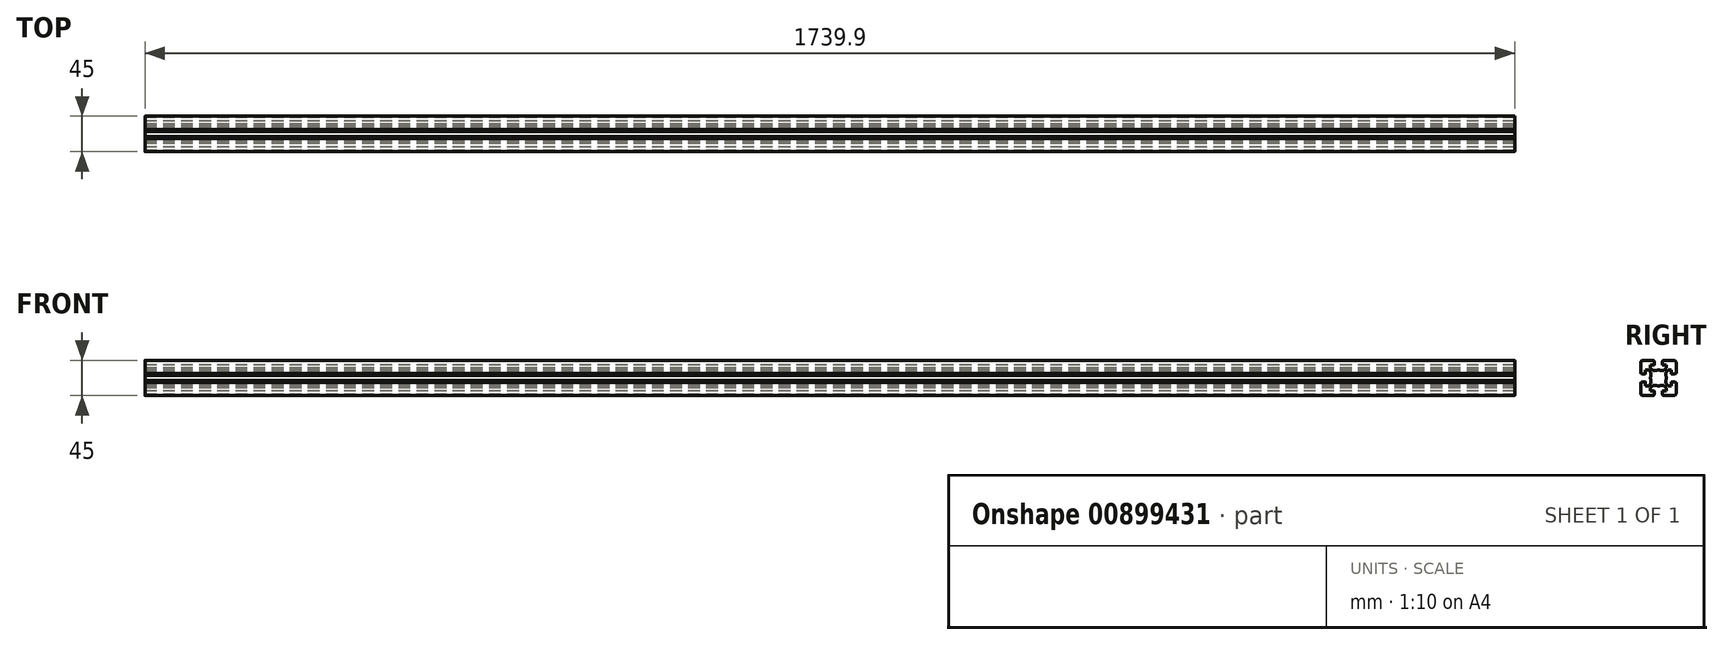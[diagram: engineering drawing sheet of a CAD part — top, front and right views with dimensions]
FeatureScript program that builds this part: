
annotation { "Feature Type Name" : "Feature", "Feature Type Description" : "" }
export const myFeature = defineFeature(function(context is Context, id is Id, definition is map)
    precondition{}
    {
        {
            var Q0;
            Q0=qCreatedBy(makeId("Right.planeOp"),FACE);
            var sketch = newSketch(context, id + "F0", { "sketchPlane" : qUnion([Q0])});
            skLineSegment(sketch, "E0", {"start": v(-20.09, -10.29) * mm, "end": v(-21.29, -10.29) * mm});
            skArc(sketch, "E1", {"start": v(-21.29, -10.29) * mm, "mid": v(-21.5, -10.38) * mm, "end": v(-21.59, -10.59) * mm});
            skLineSegment(sketch, "E2", {"start": v(-21.59, -10.59) * mm, "end": v(-21.59, -23.99) * mm});
            skArc(sketch, "E3", {"start": v(-21.59, -23.99) * mm, "mid": v(-20.7, -26.11) * mm, "end": v(-18.59, -26.99) * mm});
            skLineSegment(sketch, "E4", {"start": v(-18.59, -26.99) * mm, "end": v(-5.19, -26.99) * mm});
            skArc(sketch, "E5", {"start": v(-5.19, -26.99) * mm, "mid": v(-4.98, -26.9) * mm, "end": v(-4.89, -26.69) * mm});
            skLineSegment(sketch, "E6", {"start": v(-4.89, -26.69) * mm, "end": v(-4.89, -25.49) * mm});
            skLineSegment(sketch, "E7", {"start": v(-4.89, -25.49) * mm, "end": v(-4.39, -25.49) * mm});
            skArc(sketch, "E8", {"start": v(-4.39, -25.49) * mm, "mid": v(-4.18, -25.4) * mm, "end": v(-4.09, -25.19) * mm});
            skLineSegment(sketch, "E9", {"start": v(-4.09, -25.19) * mm, "end": v(-4.09, -21.29) * mm});
            skArc(sketch, "E10", {"start": v(-4.09, -21.29) * mm, "mid": v(-4.18, -21.08) * mm, "end": v(-4.39, -20.99) * mm});
            skLineSegment(sketch, "E11", {"start": v(-4.39, -20.99) * mm, "end": v(-9.14, -20.99) * mm});
            skLineSegment(sketch, "E12", {"start": v(-9.14, -20.99) * mm, "end": v(-9.14, -16.88) * mm});
            skLineSegment(sketch, "E13", {"start": v(-9.14, -16.88) * mm, "end": v(-6.25, -13.99) * mm});
            skLineSegment(sketch, "E14", {"start": v(-6.25, -13.99) * mm, "end": v(-2.21, -13.99) * mm});
            skArc(sketch, "E15", {"start": v(-2.21, -13.99) * mm, "mid": v(0.91, -14.49) * mm, "end": v(4.03, -13.99) * mm});
            skLineSegment(sketch, "E16", {"start": v(-20.09, -10.29) * mm, "end": v(-20.09, -9.79) * mm});
            skArc(sketch, "E17", {"start": v(-20.09, -9.79) * mm, "mid": v(-20, -9.58) * mm, "end": v(-19.79, -9.49) * mm});
            skLineSegment(sketch, "E18", {"start": v(-19.79, -9.49) * mm, "end": v(-15.89, -9.49) * mm});
            skArc(sketch, "E19", {"start": v(-15.89, -9.49) * mm, "mid": v(-15.68, -9.58) * mm, "end": v(-15.59, -9.79) * mm});
            skLineSegment(sketch, "E20", {"start": v(-15.59, -9.79) * mm, "end": v(-15.59, -14.54) * mm});
            skLineSegment(sketch, "E21", {"start": v(-15.59, -14.54) * mm, "end": v(-11.48, -14.54) * mm});
            skLineSegment(sketch, "E22", {"start": v(-11.48, -14.54) * mm, "end": v(-8.59, -11.65) * mm});
            skLineSegment(sketch, "E23", {"start": v(-8.59, -11.65) * mm, "end": v(-8.59, -7.61) * mm});
            skLineSegment(sketch, "E24", {"start": v(29.82, -4.49) * mm, "end": v(-31.05, -4.49) * mm});
            skLineSegment(sketch, "E25.MirrorCS", {"start": v(6.71, -25.49) * mm, "end": v(6.21, -25.49) * mm});
            skArc(sketch, "E26.MirrorCS", {"start": v(7.01, -26.99) * mm, "mid": v(6.8, -26.9) * mm, "end": v(6.71, -26.69) * mm});
            skLineSegment(sketch, "E27.MirrorCS", {"start": v(10.41, -11.65) * mm, "end": v(10.41, -7.61) * mm});
            skArc(sketch, "E28.MirrorCS", {"start": v(6.21, -25.49) * mm, "mid": v(6, -25.4) * mm, "end": v(5.91, -25.19) * mm});
            skLineSegment(sketch, "E29.MirrorCS", {"start": v(6.71, -26.69) * mm, "end": v(6.71, -25.49) * mm});
            skArc(sketch, "E30.MirrorCS", {"start": v(5.91, -21.29) * mm, "mid": v(6, -21.08) * mm, "end": v(6.21, -20.99) * mm});
            skLineSegment(sketch, "E31.MirrorCS", {"start": v(10.96, -16.88) * mm, "end": v(8.07, -13.99) * mm});
            skLineSegment(sketch, "E32.MirrorCS", {"start": v(13.3, -14.54) * mm, "end": v(10.41, -11.65) * mm});
            skLineSegment(sketch, "E33.MirrorCS", {"start": v(17.41, -14.54) * mm, "end": v(13.3, -14.54) * mm});
            skLineSegment(sketch, "E34.MirrorCS", {"start": v(17.41, -9.79) * mm, "end": v(17.41, -14.54) * mm});
            skLineSegment(sketch, "E35.MirrorCS", {"start": v(6.21, -20.99) * mm, "end": v(10.96, -20.99) * mm});
            skLineSegment(sketch, "E36.MirrorCS", {"start": v(8.07, -13.99) * mm, "end": v(4.03, -13.99) * mm});
            skArc(sketch, "E37.MirrorCS", {"start": v(4.03, -13.99) * mm, "mid": v(0.91, -14.49) * mm, "end": v(-2.21, -13.99) * mm});
            skLineSegment(sketch, "E38.MirrorCS", {"start": v(10.96, -20.99) * mm, "end": v(10.96, -16.88) * mm});
            skLineSegment(sketch, "E39.MirrorCS", {"start": v(5.91, -25.19) * mm, "end": v(5.91, -21.29) * mm});
            skArc(sketch, "E40.MirrorCS", {"start": v(23.41, -23.99) * mm, "mid": v(22.53, -26.11) * mm, "end": v(20.41, -26.99) * mm});
            skLineSegment(sketch, "E41.MirrorCS", {"start": v(20.41, -26.99) * mm, "end": v(7.01, -26.99) * mm});
            skLineSegment(sketch, "E42.MirrorCS", {"start": v(23.41, -10.59) * mm, "end": v(23.41, -23.99) * mm});
            skArc(sketch, "E43.MirrorCS", {"start": v(17.71, -9.49) * mm, "mid": v(17.5, -9.58) * mm, "end": v(17.41, -9.79) * mm});
            skArc(sketch, "E44.MirrorCS", {"start": v(23.11, -10.29) * mm, "mid": v(23.32, -10.38) * mm, "end": v(23.41, -10.59) * mm});
            skLineSegment(sketch, "E45.MirrorCS", {"start": v(21.91, -10.29) * mm, "end": v(21.91, -9.79) * mm});
            skLineSegment(sketch, "E46.MirrorCS", {"start": v(21.91, -10.29) * mm, "end": v(23.11, -10.29) * mm});
            skArc(sketch, "E47.MirrorCS", {"start": v(21.91, -9.79) * mm, "mid": v(21.82, -9.58) * mm, "end": v(21.61, -9.49) * mm});
            skLineSegment(sketch, "E48.MirrorCS", {"start": v(21.61, -9.49) * mm, "end": v(17.71, -9.49) * mm});
            skLineSegment(sketch, "E49.MirrorCS", {"start": v(6.71, 16.51) * mm, "end": v(6.21, 16.51) * mm});
            skArc(sketch, "E50.MirrorCS", {"start": v(-4.39, 16.51) * mm, "mid": v(-4.18, 16.42) * mm, "end": v(-4.09, 16.21) * mm});
            skLineSegment(sketch, "E51.MirrorCS", {"start": v(-4.89, 16.51) * mm, "end": v(-4.39, 16.51) * mm});
            skArc(sketch, "E52.MirrorCS", {"start": v(5.91, 12.31) * mm, "mid": v(6, 12.1) * mm, "end": v(6.21, 12.01) * mm});
            skLineSegment(sketch, "E53.MirrorCS", {"start": v(6.71, 17.71) * mm, "end": v(6.71, 16.51) * mm});
            skLineSegment(sketch, "E54.MirrorCS", {"start": v(-4.89, 17.71) * mm, "end": v(-4.89, 16.51) * mm});
            skArc(sketch, "E55.MirrorCS", {"start": v(-5.19, 18.01) * mm, "mid": v(-4.98, 17.92) * mm, "end": v(-4.89, 17.71) * mm});
            skArc(sketch, "E56.MirrorCS", {"start": v(-4.09, 12.31) * mm, "mid": v(-4.18, 12.1) * mm, "end": v(-4.39, 12.01) * mm});
            skArc(sketch, "E57.MirrorCS", {"start": v(7.01, 18.01) * mm, "mid": v(6.8, 17.92) * mm, "end": v(6.71, 17.71) * mm});
            skArc(sketch, "E58.MirrorCS", {"start": v(6.21, 16.51) * mm, "mid": v(6, 16.42) * mm, "end": v(5.91, 16.21) * mm});
            skArc(sketch, "E59.MirrorCS", {"start": v(23.11, 1.31) * mm, "mid": v(23.32, 1.4) * mm, "end": v(23.41, 1.61) * mm});
            skLineSegment(sketch, "E60.MirrorCS", {"start": v(21.91, 1.31) * mm, "end": v(21.91, 0.81) * mm});
            skArc(sketch, "E61.MirrorCS", {"start": v(-15.89, 0.51) * mm, "mid": v(-15.68, 0.6) * mm, "end": v(-15.59, 0.81) * mm});
            skArc(sketch, "E62.MirrorCS", {"start": v(-21.29, 1.31) * mm, "mid": v(-21.5, 1.4) * mm, "end": v(-21.59, 1.61) * mm});
            skArc(sketch, "E63.MirrorCS", {"start": v(17.71, 0.51) * mm, "mid": v(17.5, 0.6) * mm, "end": v(17.41, 0.81) * mm});
            skArc(sketch, "E64.MirrorCS", {"start": v(21.91, 0.81) * mm, "mid": v(21.82, 0.6) * mm, "end": v(21.61, 0.51) * mm});
            skLineSegment(sketch, "E65.MirrorCS", {"start": v(21.91, 1.31) * mm, "end": v(23.11, 1.31) * mm});
            skArc(sketch, "E66.MirrorCS", {"start": v(14.31, 5.31) * mm, "mid": v(14.1, 5.4) * mm, "end": v(14.01, 5.61) * mm});
            skArc(sketch, "E67.MirrorCS", {"start": v(-20.09, 0.81) * mm, "mid": v(-20, 0.6) * mm, "end": v(-19.79, 0.51) * mm});
            skLineSegment(sketch, "E68.MirrorCS", {"start": v(-20.09, 1.31) * mm, "end": v(-21.29, 1.31) * mm});
            skLineSegment(sketch, "E69.MirrorCS", {"start": v(-20.09, 1.31) * mm, "end": v(-20.09, 0.81) * mm});
            skLineSegment(sketch, "E70.MirrorCS", {"start": v(8.07, 5.01) * mm, "end": v(4.03, 5.01) * mm});
            skLineSegment(sketch, "E71.MirrorCS", {"start": v(-4.09, 16.21) * mm, "end": v(-4.09, 12.31) * mm});
            skLineSegment(sketch, "E72.MirrorCS", {"start": v(-9.14, 12.01) * mm, "end": v(-9.14, 7.9) * mm});
            skLineSegment(sketch, "E73.MirrorCS", {"start": v(-15.59, 5.56) * mm, "end": v(-11.48, 5.56) * mm});
            skLineSegment(sketch, "E74.MirrorCS", {"start": v(-4.39, 12.01) * mm, "end": v(-9.14, 12.01) * mm});
            skLineSegment(sketch, "E75.MirrorCS", {"start": v(-9.14, 7.9) * mm, "end": v(-6.25, 5.01) * mm});
            skLineSegment(sketch, "E76.MirrorCS", {"start": v(10.96, 12.01) * mm, "end": v(10.96, 7.9) * mm});
            skArc(sketch, "E77.MirrorCS", {"start": v(-21.59, 15.01) * mm, "mid": v(-20.7, 17.13) * mm, "end": v(-18.59, 18.01) * mm});
            skLineSegment(sketch, "E78.MirrorCS", {"start": v(23.41, 1.61) * mm, "end": v(23.41, 15.01) * mm});
            skLineSegment(sketch, "E79.MirrorCS", {"start": v(13.3, 5.56) * mm, "end": v(10.41, 2.67) * mm});
            skLineSegment(sketch, "E80.MirrorCS", {"start": v(-8.59, 2.67) * mm, "end": v(-8.59, -1.37) * mm});
            skLineSegment(sketch, "E81.MirrorCS", {"start": v(-15.59, 0.81) * mm, "end": v(-15.59, 5.56) * mm});
            skLineSegment(sketch, "E82.MirrorCS", {"start": v(10.41, 2.67) * mm, "end": v(10.41, -1.37) * mm});
            skLineSegment(sketch, "E83.MirrorCS", {"start": v(-18.59, 18.01) * mm, "end": v(-5.19, 18.01) * mm});
            skLineSegment(sketch, "E84.MirrorCS", {"start": v(10.96, 7.9) * mm, "end": v(8.07, 5.01) * mm});
            skLineSegment(sketch, "E85.MirrorCS", {"start": v(17.41, 5.56) * mm, "end": v(13.3, 5.56) * mm});
            skArc(sketch, "E86.MirrorCS", {"start": v(23.41, 15.01) * mm, "mid": v(22.53, 17.13) * mm, "end": v(20.41, 18.01) * mm});
            skLineSegment(sketch, "E87.MirrorCS", {"start": v(5.91, 16.21) * mm, "end": v(5.91, 12.31) * mm});
            skLineSegment(sketch, "E88.MirrorCS", {"start": v(17.41, 0.81) * mm, "end": v(17.41, 5.56) * mm});
            skLineSegment(sketch, "E89.MirrorCS", {"start": v(-11.48, 5.56) * mm, "end": v(-8.59, 2.67) * mm});
            skLineSegment(sketch, "E90.MirrorCS", {"start": v(-6.25, 5.01) * mm, "end": v(-2.21, 5.01) * mm});
            skLineSegment(sketch, "E91.MirrorCS", {"start": v(-21.59, 1.61) * mm, "end": v(-21.59, 15.01) * mm});
            skArc(sketch, "E92.MirrorCS", {"start": v(4.03, 5.01) * mm, "mid": v(0.91, 5.51) * mm, "end": v(-2.21, 5.01) * mm});
            skLineSegment(sketch, "E93.MirrorCS", {"start": v(6.21, 12.01) * mm, "end": v(10.96, 12.01) * mm});
            skArc(sketch, "E94.MirrorCS", {"start": v(-2.21, 5.01) * mm, "mid": v(0.91, 5.51) * mm, "end": v(4.03, 5.01) * mm});
            skLineSegment(sketch, "E95.MirrorCS", {"start": v(20.41, 18.01) * mm, "end": v(7.01, 18.01) * mm});
            skLineSegment(sketch, "E96.MirrorCS", {"start": v(-19.79, 0.51) * mm, "end": v(-15.89, 0.51) * mm});
            skLineSegment(sketch, "E97.MirrorCS", {"start": v(21.61, 0.51) * mm, "end": v(17.71, 0.51) * mm});
            skLineSegment(sketch, "E98.MirrorCS", {"start": v(0.91, -27.65) * mm, "end": v(0.91, 19.82) * mm});
            skArc(sketch, "E99", {"start": v(-8.59, -1.37) * mm, "mid": v(-9.09, -4.49) * mm, "end": v(-8.59, -7.61) * mm});
            skArc(sketch, "E100", {"start": v(10.41, -7.61) * mm, "mid": v(10.91, -4.49) * mm, "end": v(10.41, -1.37) * mm});
            skSolve(sketch);
        }
        {
            var Q0;
            Q0=qSketchRegion(id+"F0",true);
            extrude(context, id + "F1", {"entities" : qUnion([Q0]), "depth" : 1739.9 * mm, "offsetDistance" : 25.4 * mm});
        }
    });
